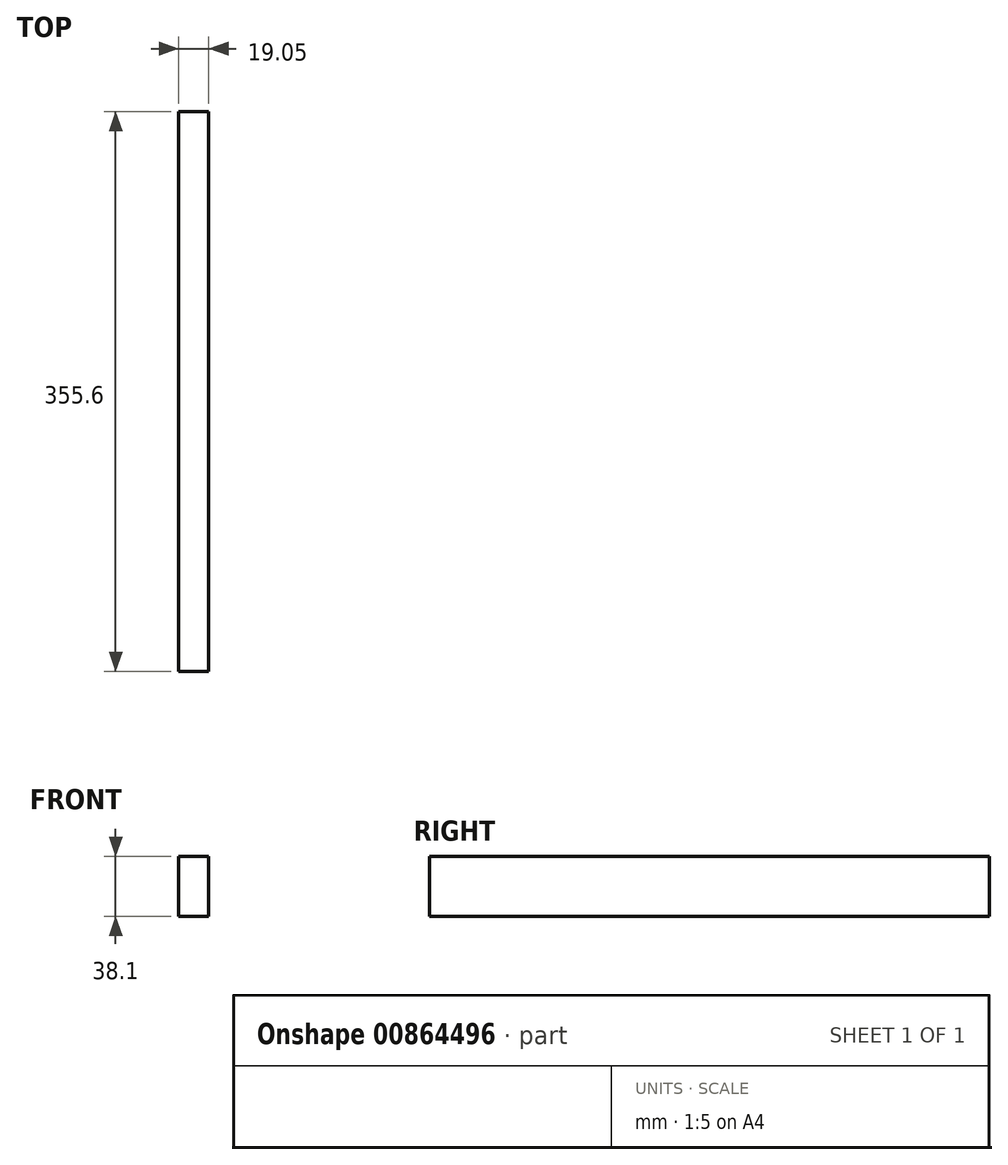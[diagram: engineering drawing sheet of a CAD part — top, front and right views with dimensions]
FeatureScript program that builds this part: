
annotation { "Feature Type Name" : "Feature", "Feature Type Description" : "" }
export const myFeature = defineFeature(function(context is Context, id is Id, definition is map)
    precondition{}
    {
        {
            var Q0;
            Q0=qCreatedBy(makeId("Right.planeOp"),FACE);
            var sketch = newSketch(context, id + "F0", { "sketchPlane" : qUnion([Q0])});
            skLineSegment(sketch, "E0.bottom", {"start": v(177.8, 19.05) * mm, "end": v(-177.8, 19.05) * mm});
            skLineSegment(sketch, "E0.top", {"start": v(177.8, -19.05) * mm, "end": v(-177.8, -19.05) * mm});
            skLineSegment(sketch, "E0.left", {"start": v(177.8, 19.05) * mm, "end": v(177.8, -19.05) * mm});
            skLineSegment(sketch, "E0.right", {"start": v(-177.8, 19.05) * mm, "end": v(-177.8, -19.05) * mm});
            skPoint(sketch, "E0.middle", {"position": v(0, 0) * mm});
            skSolve(sketch);
        }
        {
            var Q0;
            Q0=makeQuery(id+"F0.imprint","IMPRINT",FACE,{"disambiguationData":[TD([[makeQuery(id+"F0.imprint","IMPRINT",EDGE,{"derivedFrom":sQuery(id+"F0.wireOp",EDGE,"E0.bottom")}),1.0]])]});
            extrude(context, id + "F1", {"entities" : qUnion([Q0]), "depth" : 19.05 * mm, "offsetDistance" : 25.4 * mm});
        }
    });
